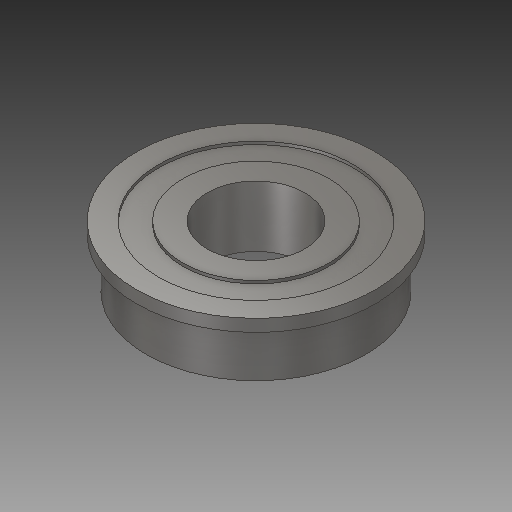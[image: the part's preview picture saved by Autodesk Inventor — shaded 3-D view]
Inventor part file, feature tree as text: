
AUTODESK INVENTOR PART (.ipt)
format: ipt  version: 2017 (Build 210142000, 142)  size: 145,408 bytes
history: native  units: in
note: dims shown in document units (in); Inventor stores cm internally (conversion verified against a paired STEP export)
features: revolve x1
ambient origin geometry x8: Origin, YZ Plane, XZ Plane, XY Plane, X Axis, Y Axis, Z Axis, Center Point
bodies: Solid1 (feature_tree)
feature tree (1):
  revolve  "Revolve1"  [1 undecoded]
note: 1 required parameter value undecoded (feature->parameter linkage not recoverable at this tier; creation-order binding heuristic only, values carry confidence <= 0.55)
